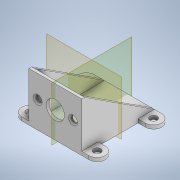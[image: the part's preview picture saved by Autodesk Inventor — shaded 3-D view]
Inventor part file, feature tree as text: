
AUTODESK INVENTOR PART (.ipt)
format: ipt  version: 2022 (Build 260153000, 153)  size: 189,440 bytes
history: native  units: mm
features: sketch x5, mirror x4, other x3, extrude x2, hole x2
ambient origin geometry x8: Origin, YZ Plane, XZ Plane, XY Plane, X Axis, Y Axis, Z Axis, Center Point
bodies: Solide1 (feature_tree)
feature tree (16):
  extrude  "Extrusion1"  Depth=2.0mm
  other  "Nervure1"
  other  "Plan de construction1"
  mirror  "Symétrie1"
  hole  "Perçage1"  [1 undecoded]
  hole  "Perçage2"  [1 undecoded]
  mirror  "Symétrie2"
  extrude  "Extrusion3"  Depth=25.0mm
  other  "Plan de construction3"
  mirror  "Symétrie3"
  mirror  "Symétrie4"
  sketch  "Esquisse1"
  sketch  "Esquisse4"
  sketch  "Esquisse5"
  sketch  "Esquisse6"
  sketch  "Esquisse7"
note: 2 required parameter values undecoded (feature->parameter linkage not recoverable at this tier; creation-order binding heuristic only, values carry confidence <= 0.55)
